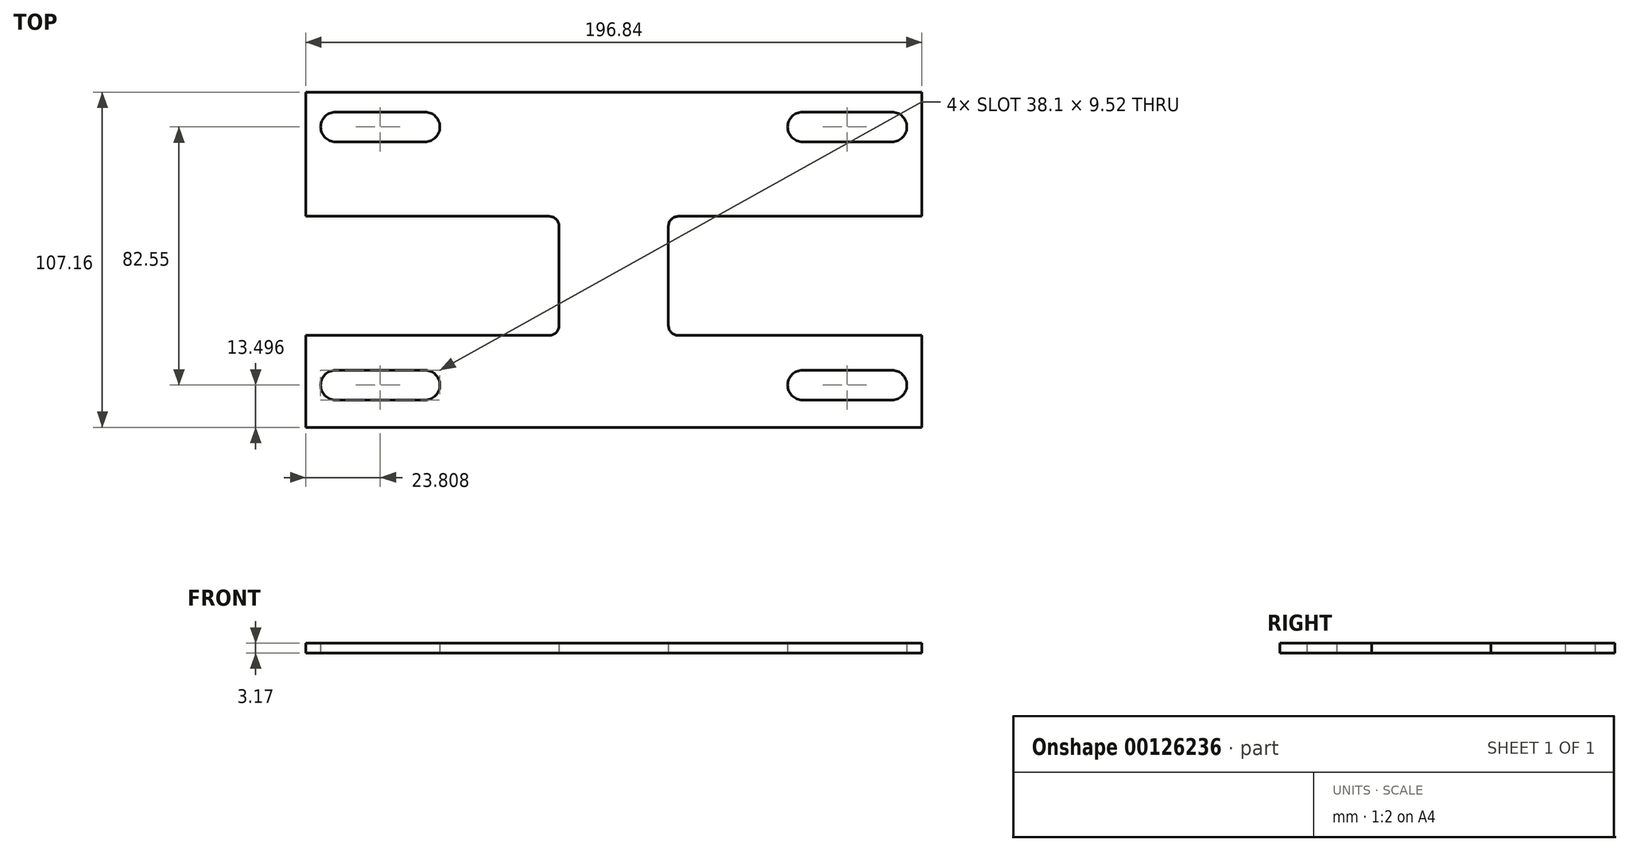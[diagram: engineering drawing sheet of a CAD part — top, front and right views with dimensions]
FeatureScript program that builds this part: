
annotation { "Feature Type Name" : "Feature", "Feature Type Description" : "" }
export const myFeature = defineFeature(function(context is Context, id is Id, definition is map)
    precondition{}
    {
        {
            var Q0;
            Q0=qCreatedBy(makeId("Top.planeOp"),FACE);
            var sketch = newSketch(context, id + "F0", { "sketchPlane" : qUnion([Q0])});
            skLineSegment(sketch, "E0.bottom", {"start": v(-98.43, -53.58) * mm, "end": v(98.43, -53.58) * mm});
            skLineSegment(sketch, "E0.top", {"start": v(-98.43, 53.58) * mm, "end": v(98.42, 53.58) * mm});
            skLineSegment(sketch, "E0.left", {"start": v(-98.43, -53.58) * mm, "end": v(-98.43, 53.58) * mm});
            skLineSegment(sketch, "E0.right", {"start": v(98.43, -53.58) * mm, "end": v(98.42, 53.58) * mm});
            skPoint(sketch, "E0.middle", {"position": v(0, 0) * mm});
            skLineSegment(sketch, "E1", {"start": v(-88.9, 42.47) * mm, "end": v(-60.33, 42.47) * mm});
            skArc(sketch, "E2.0.startCap", {"start": v(-88.9, 37.7) * mm, "mid": v(-93.66, 42.47) * mm, "end": v(-88.9, 47.23) * mm});
            skArc(sketch, "E2.0.endCap", {"start": v(-60.33, 47.23) * mm, "mid": v(-55.56, 42.47) * mm, "end": v(-60.33, 37.7) * mm});
            skLineSegment(sketch, "E2.0.left", {"start": v(-88.9, 47.23) * mm, "end": v(-60.33, 47.23) * mm});
            skLineSegment(sketch, "E2.0.right", {"start": v(-88.9, 37.7) * mm, "end": v(-60.33, 37.7) * mm});
            skLineSegment(sketch, "E3", {"start": v(-88.9, -40.08) * mm, "end": v(-60.33, -40.08) * mm});
            skArc(sketch, "E4.0.startCap", {"start": v(-88.9, -44.85) * mm, "mid": v(-93.66, -40.08) * mm, "end": v(-88.9, -35.32) * mm});
            skArc(sketch, "E4.0.endCap", {"start": v(-60.33, -35.32) * mm, "mid": v(-55.56, -40.08) * mm, "end": v(-60.33, -44.85) * mm});
            skLineSegment(sketch, "E4.0.left", {"start": v(-88.9, -35.32) * mm, "end": v(-60.33, -35.32) * mm});
            skLineSegment(sketch, "E4.0.right", {"start": v(-88.9, -44.85) * mm, "end": v(-60.33, -44.85) * mm});
            skLineSegment(sketch, "E5.MirrorCS", {"start": v(88.9, -44.85) * mm, "end": v(60.33, -44.85) * mm});
            skLineSegment(sketch, "E6.MirrorCS", {"start": v(88.9, -35.32) * mm, "end": v(60.33, -35.32) * mm});
            skArc(sketch, "E7.MirrorCS", {"start": v(60.33, -35.32) * mm, "mid": v(55.56, -40.08) * mm, "end": v(60.33, -44.85) * mm});
            skArc(sketch, "E8.MirrorCS", {"start": v(88.9, -44.85) * mm, "mid": v(93.66, -40.08) * mm, "end": v(88.9, -35.32) * mm});
            skLineSegment(sketch, "E9.MirrorCS", {"start": v(88.9, -40.08) * mm, "end": v(60.33, -40.08) * mm});
            skArc(sketch, "E10.MirrorCS", {"start": v(88.9, 37.7) * mm, "mid": v(93.66, 42.47) * mm, "end": v(88.9, 47.23) * mm});
            skArc(sketch, "E11.MirrorCS", {"start": v(60.33, 47.23) * mm, "mid": v(55.56, 42.47) * mm, "end": v(60.33, 37.7) * mm});
            skLineSegment(sketch, "E12.MirrorCS", {"start": v(88.9, 42.47) * mm, "end": v(60.33, 42.47) * mm});
            skLineSegment(sketch, "E13.MirrorCS", {"start": v(88.9, 47.23) * mm, "end": v(60.33, 47.23) * mm});
            skLineSegment(sketch, "E14.MirrorCS", {"start": v(88.9, 37.7) * mm, "end": v(60.33, 37.7) * mm});
            skLineSegment(sketch, "E15.bottom", {"start": v(-98.43, 13.9) * mm, "end": v(-20.64, 13.9) * mm});
            skLineSegment(sketch, "E15.top", {"start": v(-98.42, -24.2) * mm, "end": v(-20.64, -24.2) * mm});
            skLineSegment(sketch, "E15.left", {"start": v(-98.43, 13.9) * mm, "end": v(-98.43, -24.2) * mm});
            skLineSegment(sketch, "E15.right", {"start": v(-17.46, 10.72) * mm, "end": v(-17.46, -21.03) * mm});
            skPoint(sketch, "E16.visualSharp", {"position": v(-17.46, 13.9) * mm});
            skArc(sketch, "E16.filletArc", {"start": v(-17.46, 10.72) * mm, "mid": v(-18.4, 12.96) * mm, "end": v(-20.64, 13.9) * mm});
            skPoint(sketch, "E17.visualSharp", {"position": v(-17.46, -24.2) * mm});
            skArc(sketch, "E17.filletArc", {"start": v(-20.64, -24.2) * mm, "mid": v(-18.4, -23.28) * mm, "end": v(-17.46, -21.03) * mm});
            skArc(sketch, "E18.MirrorCS", {"start": v(20.64, -24.2) * mm, "mid": v(18.4, -23.28) * mm, "end": v(17.46, -21.03) * mm});
            skArc(sketch, "E19.MirrorCS", {"start": v(17.46, 10.72) * mm, "mid": v(18.4, 12.96) * mm, "end": v(20.64, 13.9) * mm});
            skPoint(sketch, "E20.MirrorP", {"position": v(17.46, -24.2) * mm});
            skLineSegment(sketch, "E21.MirrorCS", {"start": v(98.42, -24.2) * mm, "end": v(20.64, -24.2) * mm});
            skLineSegment(sketch, "E22.MirrorCS", {"start": v(17.46, 10.72) * mm, "end": v(17.46, -21.03) * mm});
            skLineSegment(sketch, "E23.MirrorCS", {"start": v(98.43, 13.9) * mm, "end": v(20.64, 13.9) * mm});
            skPoint(sketch, "E24.MirrorP", {"position": v(17.46, 13.9) * mm});
            skLineSegment(sketch, "E25", {"start": v(-34.92, -5.16) * mm, "end": v(-31.75, -5.16) * mm});
            skPoint(sketch, "E25.startSnap0", {"position": v(-17.46, -5.16) * mm});
            skArc(sketch, "E26.0.startCap", {"start": v(-34.92, -9.92) * mm, "mid": v(-39.69, -5.16) * mm, "end": v(-34.92, -0.4) * mm});
            skArc(sketch, "E26.0.endCap", {"start": v(-31.75, -0.4) * mm, "mid": v(-26.99, -5.16) * mm, "end": v(-31.75, -9.92) * mm});
            skLineSegment(sketch, "E26.0.left", {"start": v(-34.92, -0.4) * mm, "end": v(-31.75, -0.4) * mm});
            skLineSegment(sketch, "E26.0.right", {"start": v(-34.92, -9.92) * mm, "end": v(-31.75, -9.92) * mm});
            skLineSegment(sketch, "E27", {"start": v(34.92, -5.15) * mm, "end": v(38.1, -5.15) * mm});
            skArc(sketch, "E28.0.startCap", {"start": v(34.92, -9.92) * mm, "mid": v(30.16, -5.15) * mm, "end": v(34.92, -0.4) * mm});
            skArc(sketch, "E28.0.endCap", {"start": v(38.1, -0.4) * mm, "mid": v(42.86, -5.15) * mm, "end": v(38.1, -9.92) * mm});
            skLineSegment(sketch, "E28.0.left", {"start": v(34.92, -0.4) * mm, "end": v(38.1, -0.4) * mm});
            skLineSegment(sketch, "E28.0.right", {"start": v(34.92, -9.92) * mm, "end": v(38.1, -9.92) * mm});
            skSolve(sketch);
        }
        {
            var Q0;
            {var subQ5=sQuery(id+"F0.wireOp",EDGE,"E0.bottom");Q0=makeQuery(id+"F0.imprint","IMPRINT",FACE,{"disambiguationData":[TD([[makeQuery(id+"F0.imprint","IMPRINT",EDGE,{"derivedFrom":subQ5}),1.0]])]});}
            extrude(context, id + "F1", {"entities" : qUnion([Q0]), "depth" : 3.17 * mm});
        }
    });
